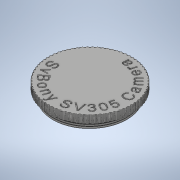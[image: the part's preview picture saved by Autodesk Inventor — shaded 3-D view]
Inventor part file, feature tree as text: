
AUTODESK INVENTOR PART (.ipt)
format: ipt  version: 2021.2 (Build 252289000, 289)  size: 9,391,616 bytes
history: native  units: in
note: dims shown in document units (in); Inventor stores cm internally (conversion verified against a paired STEP export)
features: sketch x3, extrude x2, helix x1, pattern_circular x1, plane x1, mirror x1
ambient origin geometry x8: Origin, YZ Plane, XZ Plane, XY Plane, X Axis, Y Axis, Z Axis, Center Point
bodies: Solid1 (feature_tree), Body1 (feature_tree)
feature tree (9):
  extrude  "Extrusion2"  Depth=1.75in
  extrude  "Extrusion4"  Depth=0.0344in
  helix  "Coil1"  [1 undecoded]
  pattern_circular  "Circular Pattern1"  [2 undecoded]
  plane  "Work Plane1"
  mirror  "Mirror1"
  sketch  "Sketch2"  dims[d3=0.3in d4=0.0in d8=1.75in]
  sketch  "Sketch4"  dims[d9=0.05in d10=0.0in d13=0.0344in]
  sketch  "Sketch6"  dims[d15=1.0in d16=0.25in d17=0.0492in d18=0.0in d19=90.0deg d20=90.0deg d21=0.0in d22=0.0in d23=28.3465in d24=2.4737in d26=-0.125in d27=0.0312in d6=0.5in d7=1.9685in d11=1.9685in]
note: 3 required parameter values undecoded (feature->parameter linkage not recoverable at this tier; creation-order binding heuristic only, values carry confidence <= 0.55)
